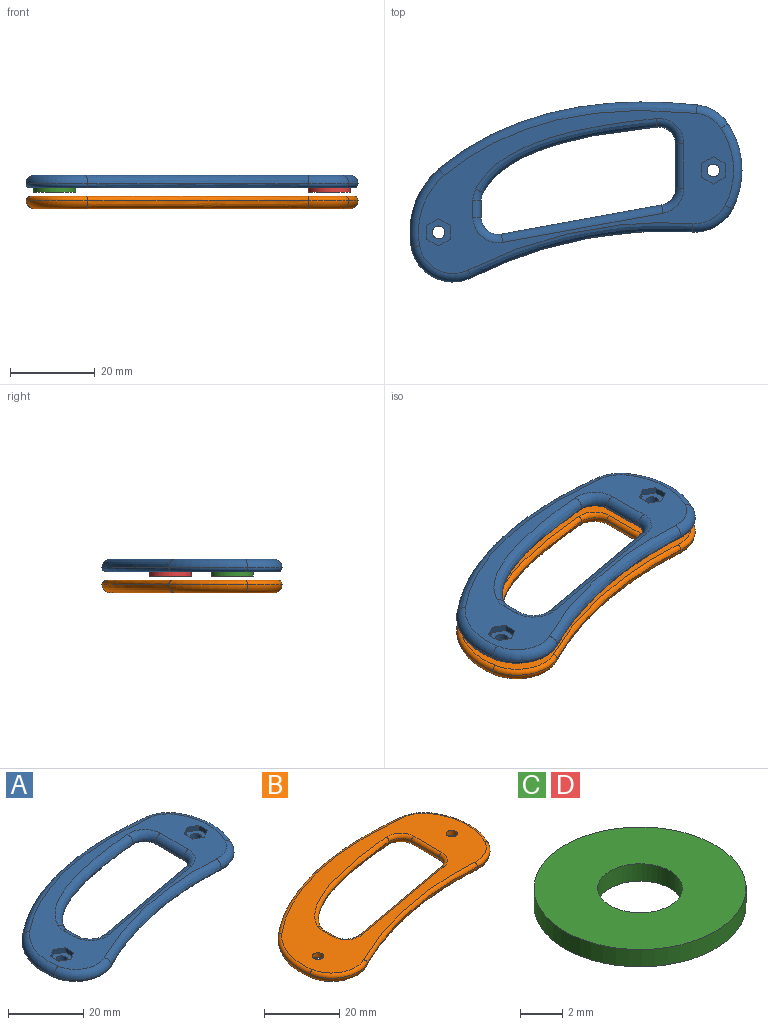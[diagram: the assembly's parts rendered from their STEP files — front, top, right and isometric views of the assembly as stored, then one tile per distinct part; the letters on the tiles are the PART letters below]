
ASSEMBLY  parts=4 mates=4
PART A: 48 faces, bbox 94.5x45.9x3.4 mm
  f0: cylinder r=1.5mm len=3mm, axis (0,0,-1), area 14.1mm2, adj f3,f32
  f1: cylinder r=1.5mm len=3mm, axis (0,0,-1), area 14.1mm2, adj f3,f25
  f2: plane 74.54x38.6mm, normal (0,0,1), area 768.6mm2, adj f4,f5,f6,f7,f8,f9,f10,f11
  f3: plane 76.54x40.6mm, normal (0,0,-1), area 1127.8mm2, adj f0,f1,f33,f34,f35,f36,f37,f38
  f4: cylinder r=2mm len=38.26mm, axis (0.98,0.18,0), area 121mm2, adj f2,f5,f6,f40
  f5: torus R=6mm, axis (0,0,1), area 26mm2, adj f2,f4,f7,f38
  f6: torus R=6mm, axis (0,0,1), area 20.7mm2, adj f2,f4,f8,f39
  f7: cylinder r=2mm len=4.04mm, axis (0,-1,0), area 12.7mm2, adj f2,f5,f9,f36
  f8: cylinder r=2mm len=10.51mm, axis (0,1,0), area 33mm2, adj f2,f6,f10,f37
  f9: torus R=6mm, axis (0,0,1), area 7mm2, adj f2,f7,f11,f34
  f10: torus R=6mm, axis (0,0,1), area 24.7mm2, adj f2,f8,f11,f35
  f11: bspline ~60.4x20.8mm, area 145mm2, adj f2,f9,f10,f33
  f12: bspline ~71.2x17.24mm, area 170.6mm2, adj f2,f13,f14,f41
  f13: torus R=8mm, axis (0,0,1), area 54.1mm2, adj f2,f12,f15,f42
  f14: torus R=8mm, axis (0,0,1), area 33.7mm2, adj f2,f12,f16,f43
  f15: torus R=18mm, axis (0,0,1), area 62mm2, adj f2,f13,f17,f44
  f16: torus R=18mm, axis (0,0,1), area 64.3mm2, adj f2,f14,f18,f45
  f17: bspline ~86.43x17.94mm, area 201.7mm2, adj f2,f15,f18,f46
  f18: torus R=8mm, axis (0,0,1), area 25.6mm2, adj f2,f16,f17,f47
  f19: plane 2.8x1.62mm, normal (-0.5,0.87,0), area 4.8mm2, adj f2,f20,f24,f25
  f20: plane 3.23x1.5mm, normal (-1,0,0), area 4.8mm2, adj f2,f19,f21,f25
  f21: plane 2.8x1.62mm, normal (-0.5,-0.87,0), area 4.8mm2, adj f2,f20,f22,f25
  f22: plane 2.8x1.62mm, normal (0.5,-0.87,0), area 4.8mm2, adj f2,f21,f23,f25
  f23: plane 3.23x1.5mm, normal (1,0,0), area 4.8mm2, adj f2,f22,f24,f25
  f24: plane 2.8x1.62mm, normal (0.5,0.87,0), area 4.8mm2, adj f2,f19,f23,f25
  f25: plane 6.47x5.6mm, normal (0,0,1), area 20.1mm2, adj f1,f19,f20,f21,f22,f23,f24
  f26: plane 2.8x1.62mm, normal (-0.5,0.87,0), area 4.8mm2, adj f2,f27,f31,f32
  f27: plane 3.23x1.5mm, normal (-1,0,0), area 4.8mm2, adj f2,f26,f28,f32
  f28: plane 2.8x1.62mm, normal (-0.5,-0.87,0), area 4.8mm2, adj f2,f27,f29,f32
  f29: plane 2.8x1.62mm, normal (0.5,-0.87,0), area 4.8mm2, adj f2,f28,f30,f32
  f30: plane 3.23x1.5mm, normal (1,0,0), area 4.8mm2, adj f2,f29,f31,f32
  f31: plane 2.8x1.62mm, normal (0.5,0.87,0), area 4.8mm2, adj f2,f26,f30,f32
  f32: plane 6.47x5.6mm, normal (0,0,1), area 20.1mm2, adj f0,f26,f27,f28,f29,f30,f31
  f33: bspline ~50.06x24.49mm, area 71.9mm2, adj f3,f11,f34,f35
  f34: torus R=5mm, axis (0,0,1), area 3.2mm2, adj f3,f9,f33,f36
  f35: torus R=5mm, axis (0,0,1), area 11.4mm2, adj f3,f10,f33,f37
  f36: cylinder r=1mm len=4.04mm, axis (0,1,0), area 6.3mm2, adj f3,f7,f34,f38
  f37: cylinder r=1mm len=10.51mm, axis (0,-1,0), area 16.5mm2, adj f3,f8,f35,f39
  f38: torus R=5mm, axis (0,0,1), area 12mm2, adj f3,f5,f36,f40
  f39: torus R=5mm, axis (0,0,1), area 9.5mm2, adj f3,f6,f37,f40
  f40: cylinder r=1mm len=38.09mm, axis (-0.98,-0.18,0), area 60.5mm2, adj f3,f4,f38,f39
  f41: bspline ~70.51x16.19mm, area 85mm2, adj f3,f12,f42,f43
  f42: torus R=9mm, axis (0,0,1), area 28.1mm2, adj f3,f13,f41,f44
  f43: torus R=9mm, axis (0,0,1), area 17.5mm2, adj f3,f14,f41,f45
  f44: torus R=19mm, axis (0,0,1), area 31.6mm2, adj f3,f15,f42,f46
  f45: torus R=19mm, axis (0,0,1), area 32.8mm2, adj f3,f16,f43,f47
  f46: bspline ~86.77x17.17mm, area 101.3mm2, adj f3,f17,f44,f47
  f47: torus R=9mm, axis (0,0,1), area 13.3mm2, adj f3,f18,f45,f46
PART B: 38 faces, bbox 94.5x45.8x3.4 mm
  f0: cylinder r=1.5mm len=3mm, axis (0,0,-1), area 14.1mm2, adj f2,f37
  f1: cylinder r=1.5mm len=3mm, axis (0,0,-1), area 14.1mm2, adj f2,f35
  f2: plane 76.54x40.61mm, normal (0,0,1), area 1127.8mm2, adj f0,f1,f4,f5,f6,f7,f8,f9
  f3: plane 74.54x38.6mm, normal (0,0,-1), area 756.6mm2, adj f19,f20,f21,f22,f23,f24,f25,f26
  f4: cylinder r=1mm len=38.09mm, axis (0.98,0.18,0), area 60.5mm2, adj f2,f5,f6,f26
  f5: torus R=5mm, axis (0,0,1), area 12mm2, adj f2,f4,f7,f24
  f6: torus R=5mm, axis (0,0,1), area 9.5mm2, adj f2,f4,f8,f25
  f7: cylinder r=1mm len=4.04mm, axis (0,-1,0), area 6.3mm2, adj f2,f5,f9,f22
  f8: cylinder r=1mm len=10.51mm, axis (0,1,0), area 16.5mm2, adj f2,f6,f10,f23
  f9: torus R=5mm, axis (0,0,1), area 3.2mm2, adj f2,f7,f11,f20
  f10: torus R=5mm, axis (0,0,1), area 11.4mm2, adj f2,f8,f11,f21
  f11: bspline ~59.86x19.92mm, area 71.9mm2, adj f2,f9,f10,f19
  f12: bspline ~70.51x16.2mm, area 85mm2, adj f2,f13,f14,f27
  f13: torus R=9mm, axis (0,0,1), area 28.1mm2, adj f2,f12,f15,f28
  f14: torus R=9mm, axis (0,0,1), area 17.5mm2, adj f2,f12,f16,f29
  f15: torus R=19mm, axis (0,0,1), area 31.6mm2, adj f2,f13,f17,f30
  f16: torus R=19mm, axis (0,0,1), area 32.8mm2, adj f2,f14,f18,f31
  f17: bspline ~86.77x17.2mm, area 101.3mm2, adj f2,f15,f18,f32
  f18: torus R=9mm, axis (0,0,1), area 13.3mm2, adj f2,f16,f17,f33
  f19: bspline ~60.4x20.8mm, area 145mm2, adj f3,f11,f20,f21
  f20: torus R=6mm, axis (0,0,1), area 7mm2, adj f3,f9,f19,f22
  f21: torus R=6mm, axis (0,0,1), area 24.7mm2, adj f3,f10,f19,f23
  f22: cylinder r=2mm len=4.04mm, axis (0,1,0), area 12.7mm2, adj f3,f7,f20,f24
  f23: cylinder r=2mm len=10.51mm, axis (0,-1,0), area 33mm2, adj f3,f8,f21,f25
  f24: torus R=6mm, axis (0,0,1), area 26mm2, adj f3,f5,f22,f26
  f25: torus R=6mm, axis (0,0,1), area 20.7mm2, adj f3,f6,f23,f26
  f26: cylinder r=2mm len=38.26mm, axis (-0.98,-0.18,0), area 121mm2, adj f3,f4,f24,f25
  f27: bspline ~64.82x14.04mm, area 170.6mm2, adj f3,f12,f28,f29
  f28: torus R=8mm, axis (0,0,1), area 54.1mm2, adj f3,f13,f27,f30
  f29: torus R=8mm, axis (0,0,1), area 33.7mm2, adj f3,f14,f27,f31
  f30: torus R=18mm, axis (0,0,1), area 62mm2, adj f3,f15,f28,f32
  f31: torus R=18mm, axis (0,0,1), area 64.3mm2, adj f3,f16,f29,f33
  f32: bspline ~68.04x17.94mm, area 201.7mm2, adj f3,f17,f30,f33
  f33: torus R=8mm, axis (0,0,1), area 25.6mm2, adj f3,f18,f31,f32
  f34: cylinder r=3.25mm len=6.5mm, axis (0,0,-1), area 30.6mm2, adj f3,f35
  f35: plane 6.5x6.5mm, normal (0,0,-1), area 26.1mm2, adj f1,f34
  f36: cylinder r=3.25mm len=6.5mm, axis (0,0,-1), area 30.6mm2, adj f3,f37
  f37: plane 6.5x6.5mm, normal (0,0,-1), area 26.1mm2, adj f0,f36
PART C: 4 faces, bbox 10x10x1 mm
  f0: cylinder r=2mm len=4mm, axis (0,0,-1), area 12.6mm2, adj f2,f3
  f1: cylinder r=5mm len=10mm, axis (0,0,-1), area 31.4mm2, adj f2,f3
  f2: plane 10x10mm, normal (0,0,1), area 66mm2, adj f0,f1
  f3: plane 10x10mm, normal (0,0,-1), area 66mm2, adj f0,f1
PART D: same geometry as C
PLACE A t=(0,0,18.3)mm
PLACE B t=(0,0,13.3)mm
PLACE C rot(axis=(1,0,0),180deg) t=(-30.83,-9.57,18.3)mm
PLACE D rot(axis=(1,0,0),180deg) t=(34.17,5.08,18.3)mm
MATE parallel B.f2 <-> A.f3  axis (0,0,1) through (0.5,1.32,16.3)mm
MATE cylindrical C.f1 <-> A.f0  axis (0,0,1) through (-30.83,-9.57,18.3)mm
MATE cylindrical D.f0 <-> A.f1  axis (0,0,1) through (34.17,5.08,18.3)mm
MATE slider B.f1 <-> D.f1  axis (0,0,1) through (34.17,5.08,16.3)mm
